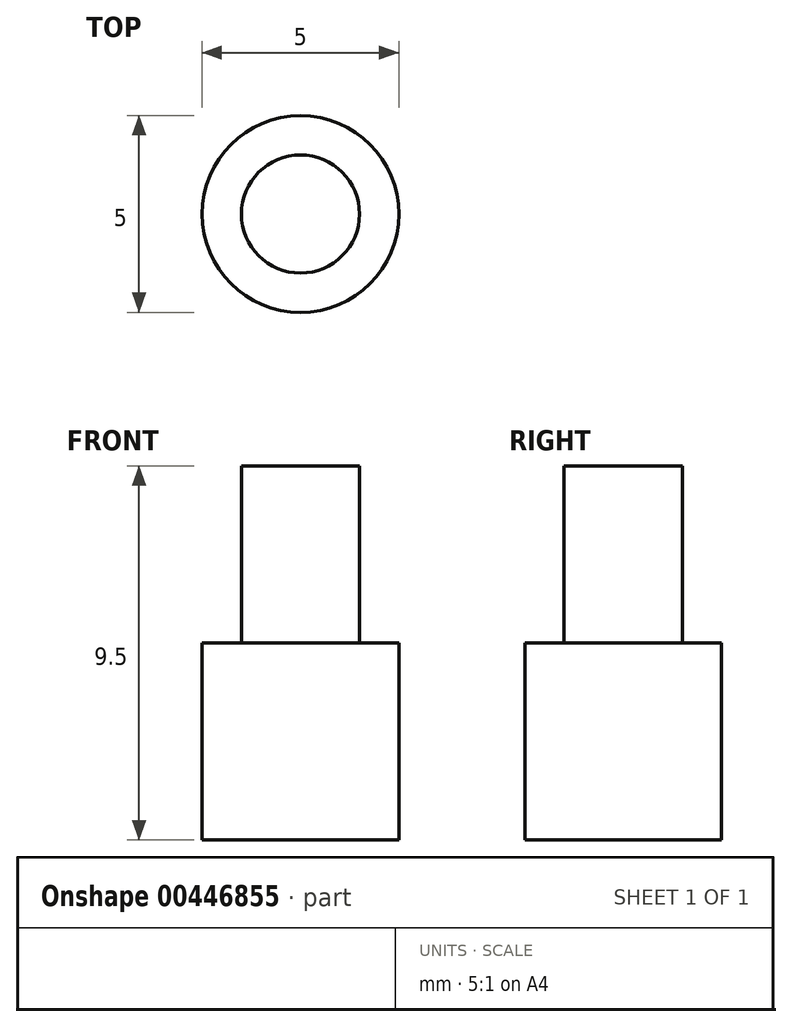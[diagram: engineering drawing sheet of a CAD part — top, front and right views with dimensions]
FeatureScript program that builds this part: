
annotation { "Feature Type Name" : "Feature", "Feature Type Description" : "" }
export const myFeature = defineFeature(function(context is Context, id is Id, definition is map)
    precondition{}
    {
        {
            var Q0;
            Q0=qCreatedBy(makeId("Top.planeOp"),FACE);
            var sketch = newSketch(context, id + "F0", { "sketchPlane" : qUnion([Q0])});
            skCircle(sketch, "E0", {"center": v(0, 0) * mm, "radius": 1.5 * mm});
            skCircle(sketch, "E1", {"center": v(0, 0) * mm, "radius": 0.5 * mm});
            skSolve(sketch);
        }
        {
            var Q0;
            Q0=makeQuery(id+"F0.imprint","IMPRINT",FACE,{"disambiguationData":[TD([[makeQuery(id+"F0.imprint","IMPRINT",EDGE,{"derivedFrom":sQuery(id+"F0.wireOp",EDGE,"E0")}),1.0]])]});
            var Q1;
            Q1=makeQuery(id+"F0.imprint","IMPRINT",FACE,{"disambiguationData":[TD([[makeQuery(id+"F0.imprint","IMPRINT",EDGE,{"derivedFrom":sQuery(id+"F0.wireOp",EDGE,"E1")}),1.0]])]});
            extrude(context, id + "F1", {"entities" : qUnion([Q0, Q1]), "oppositeDirection" : true, "depth" : 4.5 * mm});
        }
        {
            var Q0;
            Q0=makeQuery(id+"F1.opExtrude","CAP_FACE",FACE,{"disambiguationData":[OSD([sQuery(id+"F0.wireOp",EDGE,"E0"),sQuery(id+"F0.wireOp",EDGE,"E1")])],"isStart":false});
            var sketch = newSketch(context, id + "F2", { "sketchPlane" : qUnion([Q0])});
            skCircle(sketch, "E2", {"center": v(0, 0) * mm, "radius": 2.5 * mm});
            skCircle(sketch, "E3.0", {"center": v(0, 0) * mm, "radius": 1.5 * mm});
            skSolve(sketch);
        }
        {
            var Q0;
            Q0=makeQuery(id+"F2.imprint","IMPRINT",FACE,{"disambiguationData":[TD([[makeQuery(id+"F2.imprint","IMPRINT",EDGE,{"derivedFrom":sQuery(id+"F2.wireOp",EDGE,"E2")}),1.0]])]});
            var Q1;
            Q1=makeQuery(id+"F2.imprint","IMPRINT",FACE,{"disambiguationData":[TD([[makeQuery(id+"F2.imprint","IMPRINT",EDGE,{"derivedFrom":makeQuery(id+"F1.opExtrude","CAP_EDGE",EDGE,{"disambiguationData":[OSD([sQuery(id+"F0.wireOp",EDGE,"E0")])],"isStart":false})}),1.0]])]});
            var Q2;
            Q2=makeQuery(id+"F2.imprint","IMPRINT",FACE,{"disambiguationData":[TD([[makeQuery(id+"F2.imprint","IMPRINT",EDGE,{"derivedFrom":makeQuery(id+"F1.opExtrude","CAP_EDGE",EDGE,{"disambiguationData":[OSD([sQuery(id+"F0.wireOp",EDGE,"E1")])],"isStart":false})}),1.0]])]});
            var Q3;
            Q3=makeQuery(id+"F2.imprint","IMPRINT",FACE,{"disambiguationData":[TD([[makeQuery(id+"F2.imprint","IMPRINT",EDGE,{"derivedFrom":sQuery(id+"F2.wireOp",EDGE,"E3.0")}),-1.0]])]});
            extrude(context, id + "F3", {"entities" : qUnion([Q0, Q1, Q2, Q3]), "operationType" : NewBodyOperationType.ADD, "depth" : 5 * mm});
        }
    });
